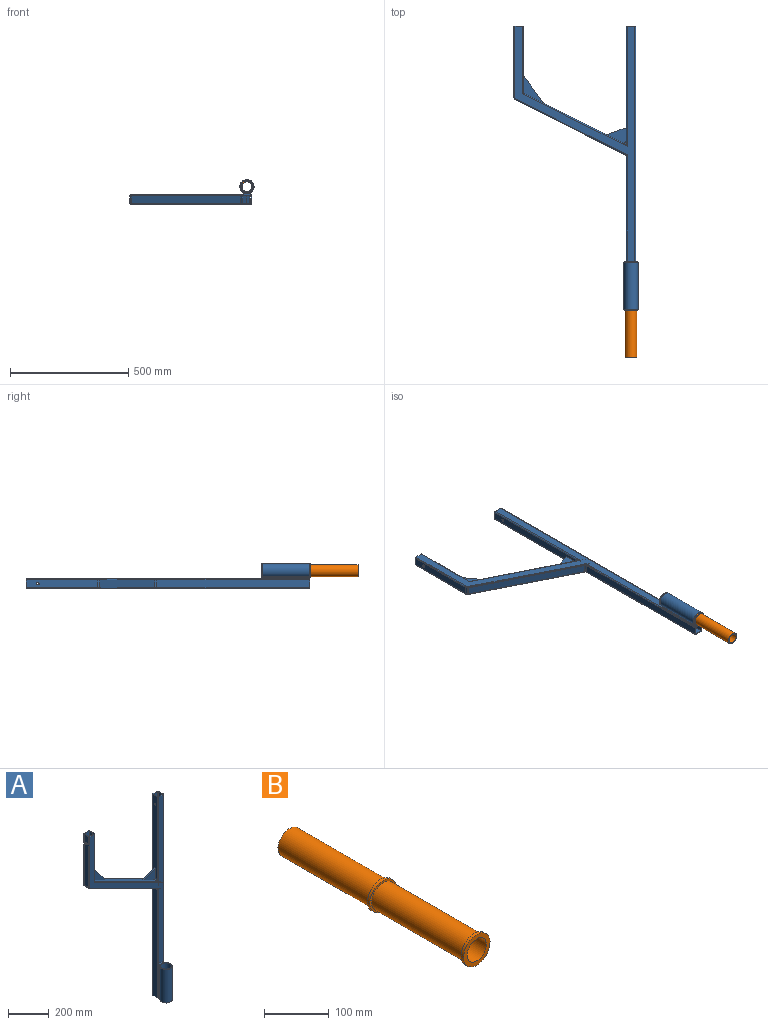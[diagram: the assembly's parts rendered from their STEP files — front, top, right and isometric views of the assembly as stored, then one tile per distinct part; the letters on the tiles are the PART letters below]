
ASSEMBLY  parts=2 mates=1
PART A: 109 faces, bbox 526x105.2x1200.2 mm
  f0: plane 995x507mm, normal (0,-1,0), area 57765.1mm2, adj f12,f24,f32,f34,f64,f65,f66,f72
  f1: plane 278.38x32mm, normal (1,0,0), area 8472.6mm2, adj f3,f64,f69,f73,f85,f90,f91,f92
  f2: plane 415.21x208.01mm, normal (0.45,0,0.89), area 14005mm2, adj f3,f4,f5,f6,f8,f65,f68,f85
  f3: cylinder r=10mm len=13.5mm, axis (0,-1,0), area 149.4mm2, adj f1,f2,f86,f91
  f4: cylinder r=10mm len=14.48mm, axis (0,-1,0), area 231.3mm2, adj f2,f6,f23,f88
  f5: cylinder r=10mm len=14.48mm, axis (0,-1,0), area 231.3mm2, adj f2,f8,f23,f89
  f6: bspline ~15.37x12.02mm, area 82.4mm2, adj f2,f4,f7,f12,f23,f65
  f7: bspline ~18.94x15.44mm, area 68.1mm2, adj f6,f12,f65
  f8: bspline ~15.37x12.02mm, area 82.4mm2, adj f2,f5,f22,f23,f68,f83
  f9: plane 1200x507mm, normal (0,1,0), area 64325.1mm2, adj f10,f21,f22,f33,f34,f64,f67,f68
  f10: cylinder r=4mm len=655.37mm, axis (0,0,1), area 4090.6mm2, adj f9,f11,f33,f80
  f11: plane 646.72x32mm, normal (-1,0,0), area 20695.1mm2, adj f10,f24,f33,f81
  f12: cylinder r=4mm len=508.84mm, axis (0,0,1), area 3111mm2, adj f0,f6,f7,f23,f34
  f13: cylinder r=1mm len=38.02mm, axis (0,0,1), area 58mm2, adj f15,f28,f41,f48
  f14: cylinder r=1mm len=504.51mm, axis (0,0,1), area 792mm2, adj f28,f30,f34,f40
  f15: plane 38.02x32mm, normal (1,0,0), area 1216.8mm2, adj f13,f17,f39,f46
  f16: plane 651.4x32mm, normal (1,0,0), area 20844.7mm2, adj f18,f29,f33,f45
  f17: cylinder r=1mm len=38.02mm, axis (0,0,1), area 58mm2, adj f15,f19,f37,f44
  f18: cylinder r=1mm len=651.4mm, axis (0,0,1), area 1022.9mm2, adj f16,f19,f33,f42
  f19: plane 1200x32mm, normal (0,-1,0), area 38217.3mm2, adj f17,f18,f25,f31,f33,f34,f35,f36
  f20: plane 1200x32mm, normal (1,0,0), area 38305mm2, adj f21,f32,f33,f34,f108
  f21: cylinder r=4mm len=1200mm, axis (0,0,1), area 7539.8mm2, adj f9,f20,f33,f34
  f22: cylinder r=4mm len=508.84mm, axis (0,0,1), area 3111mm2, adj f8,f9,f23,f34,f83
  f23: plane 486.39x32.21mm, normal (-1,0,0), area 15184.7mm2, adj f4,f5,f6,f8,f12,f22,f34,f87
  f24: cylinder r=4mm len=655.37mm, axis (0,0,1), area 3600.2mm2, adj f0,f11,f33,f82,f102,f104
  f25: cylinder r=1mm len=1200mm, axis (0,0,1), area 1885mm2, adj f19,f26,f33,f34
  f26: plane 1200x32mm, normal (-1,0,0), area 38305mm2, adj f25,f27,f33,f34,f108
  f27: cylinder r=1mm len=1200mm, axis (0,0,1), area 1885mm2, adj f26,f28,f33,f34
  f28: plane 1200x32mm, normal (0,1,0), area 38217.3mm2, adj f13,f14,f27,f29,f33,f34,f36,f40
  f29: cylinder r=1mm len=651.4mm, axis (0,0,1), area 1022.9mm2, adj f16,f28,f33,f47
  f30: plane 503.87x32mm, normal (1,0,0), area 16028.8mm2, adj f14,f31,f34,f38,f107
  f31: cylinder r=1mm len=504.51mm, axis (0,0,1), area 792mm2, adj f19,f30,f34,f35
  f32: cylinder r=4mm len=1200mm, axis (0,0,1), area 7056.8mm2, adj f0,f20,f33,f34,f100,f101
  f33: plane 105x60mm, normal (0,0,-1), area 1348mm2, adj f9,f10,f11,f16,f18,f19,f20,f21
  f34: plane 40x40mm, normal (0,0,1), area 431.1mm2, adj f0,f9,f12,f14,f19,f20,f21,f22
  f35: cylinder r=4mm len=31.1mm, axis (0.89,0,-0.45), area 34.5mm2, adj f19,f31,f36,f38
  f36: plane 34x3.58mm, normal (0.89,0,-0.45), area 102.3mm2, adj f19,f28,f35,f37,f38,f39,f40,f41
  f37: cylinder r=1mm len=30.14mm, axis (0.89,0,-0.45), area 50.9mm2, adj f17,f19,f36,f39
  f38: plane 32x31.04mm, normal (0.45,0,0.89), area 1110.8mm2, adj f30,f35,f36,f40
  f39: plane 32x29.7mm, normal (-0.45,0,-0.89), area 1062.8mm2, adj f15,f36,f37,f41
  f40: cylinder r=4mm len=31.1mm, axis (0.89,0,-0.45), area 34.5mm2, adj f14,f28,f36,f38
  f41: cylinder r=1mm len=30.14mm, axis (0.89,0,-0.45), area 50.9mm2, adj f13,f28,f36,f39
  f42: cylinder r=4mm len=13.19mm, axis (0.89,0,-0.45), area 14.3mm2, adj f18,f19,f43,f45
  f43: plane 34x3.58mm, normal (0.89,0,-0.45), area 102.3mm2, adj f19,f28,f42,f44,f45,f46,f47,f48
  f44: cylinder r=1mm len=14.92mm, axis (0.89,0,-0.45), area 24.9mm2, adj f17,f19,f43,f46
  f45: plane 32x13.13mm, normal (-0.45,0,-0.89), area 469.9mm2, adj f16,f42,f43,f47
  f46: plane 32x14.47mm, normal (0.45,0,0.89), area 518mm2, adj f15,f43,f44,f48
  f47: cylinder r=4mm len=13.19mm, axis (0.89,0,-0.45), area 14.3mm2, adj f28,f29,f43,f45
  f48: cylinder r=1mm len=14.92mm, axis (0.89,0,-0.45), area 24.9mm2, adj f13,f28,f43,f46
  f49: plane 472x236.34mm, normal (0.45,0,0.89), area 16891.7mm2, adj f52,f53,f61,f75
  f50: plane 438x219.32mm, normal (-0.45,0,-0.89), area 15674.9mm2, adj f54,f55,f57,f75
  f51: plane 463.95x232.31mm, normal (-0.45,0,-0.89), area 16603.7mm2, adj f66,f67,f78,f81
  f52: cylinder r=1mm len=472.45mm, axis (0.89,0,-0.45), area 828.4mm2, adj f49,f62,f63,f76
  f53: cylinder r=1mm len=472.45mm, axis (0.89,0,-0.45), area 828.4mm2, adj f49,f59,f60,f74
  f54: cylinder r=1mm len=439.57mm, axis (0.89,0,-0.45), area 770.4mm2, adj f50,f58,f59,f74
  f55: cylinder r=1mm len=439.57mm, axis (0.89,0,-0.45), area 770.4mm2, adj f50,f56,f63,f76
  f56: cylinder r=1mm len=287.02mm, axis (0,0,-1), area 450.4mm2, adj f55,f57,f63,f64
  f57: plane 286.41x32mm, normal (-1,0,0), area 9070mm2, adj f50,f56,f58,f64,f106
  f58: cylinder r=1mm len=287.02mm, axis (0,0,-1), area 450.4mm2, adj f54,f57,f59,f64
  f59: plane 542.69x471.13mm, normal (0,1,0), area 25788.8mm2, adj f53,f54,f58,f60,f64,f74
  f60: cylinder r=1mm len=307.41mm, axis (0,0,-1), area 482.4mm2, adj f53,f59,f61,f64
  f61: plane 307.41x32mm, normal (1,0,0), area 9742mm2, adj f49,f60,f62,f64,f105
  f62: cylinder r=1mm len=307.41mm, axis (0,0,-1), area 482.4mm2, adj f52,f61,f63,f64
  f63: plane 542.69x471.13mm, normal (0,-1,0), area 25788.8mm2, adj f52,f55,f56,f62,f64,f76
  f64: plane 40x40mm, normal (0,0,1), area 431.1mm2, adj f0,f1,f9,f56,f57,f58,f59,f60
  f65: cylinder r=4mm len=444.79mm, axis (0.89,0,-0.45), area 2999.5mm2, adj f0,f2,f6,f7,f86
  f66: cylinder r=4mm len=473.48mm, axis (0.89,0,-0.45), area 3287.3mm2, adj f0,f51,f79,f82
  f67: cylinder r=4mm len=473.48mm, axis (0.89,0,-0.45), area 3287.3mm2, adj f9,f51,f77,f80
  f68: cylinder r=4mm len=444.79mm, axis (0.89,0,-0.45), area 2999.5mm2, adj f2,f8,f9,f83,f84
  f69: cylinder r=4mm len=287.02mm, axis (0,0,-1), area 1776.3mm2, adj f1,f9,f64,f84
  f70: cylinder r=4mm len=303.08mm, axis (0,0,-1), area 1904.3mm2, adj f9,f64,f71,f77
  f71: plane 303.08x32mm, normal (-1,0,0), area 9603.6mm2, adj f64,f70,f72,f78,f105
  f72: cylinder r=4mm len=303.08mm, axis (0,0,-1), area 1904.3mm2, adj f0,f64,f71,f79
  f73: cylinder r=4mm len=287.02mm, axis (0,0,-1), area 1776.3mm2, adj f0,f1,f64,f86
  f74: cylinder r=4mm len=38.02mm, axis (0,0,1), area 37.3mm2, adj f53,f54,f59,f75
  f75: plane 38.02x32mm, normal (-1,0,0), area 1216.8mm2, adj f49,f50,f74,f76
  f76: cylinder r=4mm len=38.02mm, axis (0,0,1), area 37.3mm2, adj f52,f55,f63,f75
  f77: torus R=6mm, axis (0,-1,0), area 59.4mm2, adj f9,f67,f70,f78
  f78: cylinder r=10mm len=32mm, axis (0,-1,0), area 354.1mm2, adj f51,f71,f77,f79
  f79: torus R=6mm, axis (0,-1,0), area 59.4mm2, adj f0,f66,f72,f78
  f80: bspline ~9.52x8.94mm, area 50.6mm2, adj f10,f67,f81
  f81: cylinder r=10mm len=32mm, axis (0,1,0), area 354.1mm2, adj f11,f51,f80,f82
  f82: bspline ~9.52x8.94mm, area 48.9mm2, adj f24,f66,f81
  f83: bspline ~18.94x15.44mm, area 68.1mm2, adj f8,f22,f68
  f84: bspline ~9.52x8.94mm, area 48.9mm2, adj f68,f69,f85
  f85: cylinder r=10mm len=13.5mm, axis (0,-1,0), area 149.4mm2, adj f1,f2,f84,f92
  f86: bspline ~9.52x8.94mm, area 27.6mm2, adj f3,f65,f73
  f87: plane 84.15x29.63mm, normal (-0.33,0,0.94), area 446.1mm2, adj f2,f23,f88,f89
  f88: plane 84.15x65.58mm, normal (0,-1,0), area 2959.7mm2, adj f2,f4,f23,f87
  f89: plane 84.15x65.58mm, normal (0,1,0), area 2959.7mm2, adj f2,f5,f23,f87
  f90: plane 117.98x87.28mm, normal (0.8,0,0.59), area 733.8mm2, adj f1,f2,f91,f92
  f91: plane 117.98x87.28mm, normal (0,-1,0), area 3234.9mm2, adj f1,f2,f3,f90
  f92: plane 117.98x87.28mm, normal (0,1,0), area 3234.9mm2, adj f1,f2,f85,f90
  f93: plane 200.24x3.52mm, normal (-1,0,0), area 703.5mm2, adj f33,f97,f99,f102,f103
  f94: plane 200.24x3.52mm, normal (1,0,0), area 703.5mm2, adj f33,f97,f98,f100,f103
  f95: cylinder r=30mm len=200mm, axis (0,0,-1), area 29977.1mm2, adj f33,f97,f98,f99
  f96: cylinder r=26mm len=200mm, axis (0,0,-1), area 32672.6mm2, adj f33,f97
  f97: plane 60x60mm, normal (0,0,1), area 753.4mm2, adj f93,f94,f95,f96,f98,f99,f103
  f98: cylinder r=5mm len=200mm, axis (0,0,-1), area 927.3mm2, adj f33,f94,f95,f97
  f99: cylinder r=5mm len=200mm, axis (0,0,-1), area 927.3mm2, adj f33,f93,f95,f97
  f100: cylinder r=5mm len=205mm, axis (0,0,1), area 994.6mm2, adj f32,f33,f94,f101
  f101: torus R=9mm, axis (0,0,-1), area 8.6mm2, adj f32,f100,f103
  f102: cylinder r=5mm len=205mm, axis (0,0,1), area 994.6mm2, adj f24,f33,f93,f104
  f103: cylinder r=5mm len=32mm, axis (1,0,0), area 251.3mm2, adj f0,f93,f94,f97,f101,f104
  f104: torus R=9mm, axis (0,0,-1), area 8.6mm2, adj f24,f102,f103
  f105: cylinder r=5.5mm len=11mm, axis (1,0,0), area 103.7mm2, adj f61,f71
  f106: cylinder r=5.5mm len=11mm, axis (1,0,0), area 103.7mm2, adj f1,f57
  f107: cylinder r=5.5mm len=11mm, axis (1,0,0), area 103.7mm2, adj f23,f30
  f108: cylinder r=5.5mm len=11mm, axis (1,0,0), area 103.7mm2, adj f20,f26
PART B: 10 faces, bbox 58x410x58 mm
  f0: cylinder r=25mm len=200mm, axis (0,1,0), area 31415.9mm2, adj f4,f8
  f1: cylinder r=25mm len=200mm, axis (0,1,0), area 31415.9mm2, adj f6,f9
  f2: cylinder r=21mm len=410mm, axis (0,1,0), area 54098.2mm2, adj f3,f4
  f3: plane 58x58mm, normal (0,-1,0), area 1256.6mm2, adj f2,f5
  f4: plane 50x50mm, normal (0,1,0), area 578.1mm2, adj f0,f2
  f5: cylinder r=29mm len=58mm, axis (0,-1,0), area 911.1mm2, adj f3,f6
  f6: plane 58x58mm, normal (0,1,0), area 678.6mm2, adj f1,f5
  f7: cylinder r=29mm len=58mm, axis (0,-1,0), area 911.1mm2, adj f8,f9
  f8: plane 58x58mm, normal (0,1,0), area 678.6mm2, adj f0,f7
  f9: plane 58x58mm, normal (0,-1,0), area 678.6mm2, adj f1,f7
PLACE A rot(axis=(-1,0,0),90deg) t=(0,528.48,-529.55)mm
PLACE B rot(axis=(1,0,0),180deg) t=(20,-671.52,-494.55)mm
MATE revolute B.f0 <-> A.f95  axis (0,-1,0) through (20,-471.52,-494.55)mm
